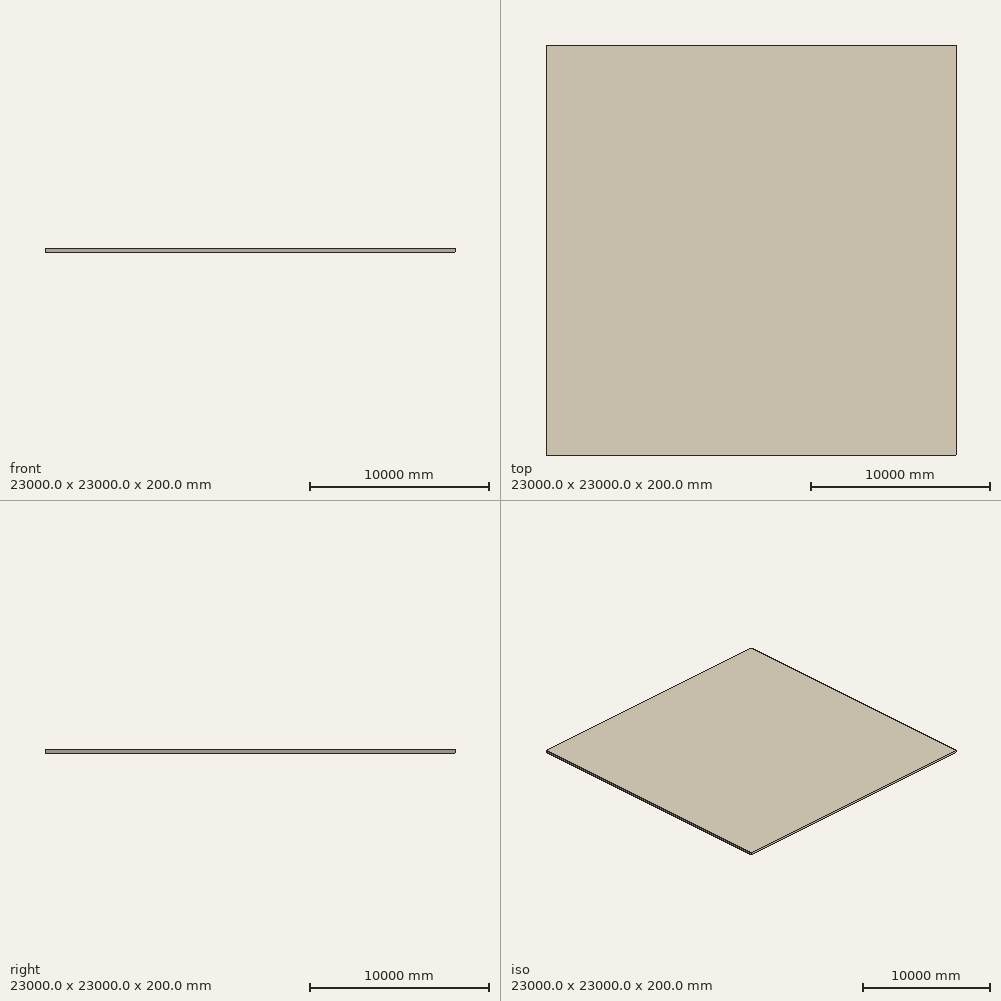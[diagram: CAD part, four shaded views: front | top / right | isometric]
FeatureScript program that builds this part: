
annotation { "Feature Type Name" : "Feature", "Feature Type Description" : "" }
export const myFeature = defineFeature(function(context is Context, id is Id, definition is map)
    precondition{}
    {
        {
            var Q0;
            Q0=qCreatedBy(makeId("Top.planeOp"),FACE);
            var sketch = newSketch(context, id + "F0", { "sketchPlane" : qUnion([Q0])});
            skLineSegment(sketch, "E0.bottom", {"start": v(0, 0) * mm, "end": v(23000, 0) * mm});
            skLineSegment(sketch, "E0.top", {"start": v(0, 23000) * mm, "end": v(23000, 23000) * mm});
            skLineSegment(sketch, "E0.left", {"start": v(0, 0) * mm, "end": v(0, 23000) * mm});
            skLineSegment(sketch, "E0.right", {"start": v(23000, 0) * mm, "end": v(23000, 23000) * mm});
            skSolve(sketch);
        }
        {
            var Q0;
            Q0=makeQuery(id+"F0.imprint","IMPRINT",FACE,{"disambiguationData":[TD([[makeQuery(id+"F0.imprint","IMPRINT",EDGE,{"derivedFrom":sQuery(id+"F0.wireOp",EDGE,"E0.bottom")}),1.0]])]});
            extrude(context, id + "F1", {"entities" : qUnion([Q0]), "oppositeDirection" : true, "depth" : 200 * mm});
        }
    });
